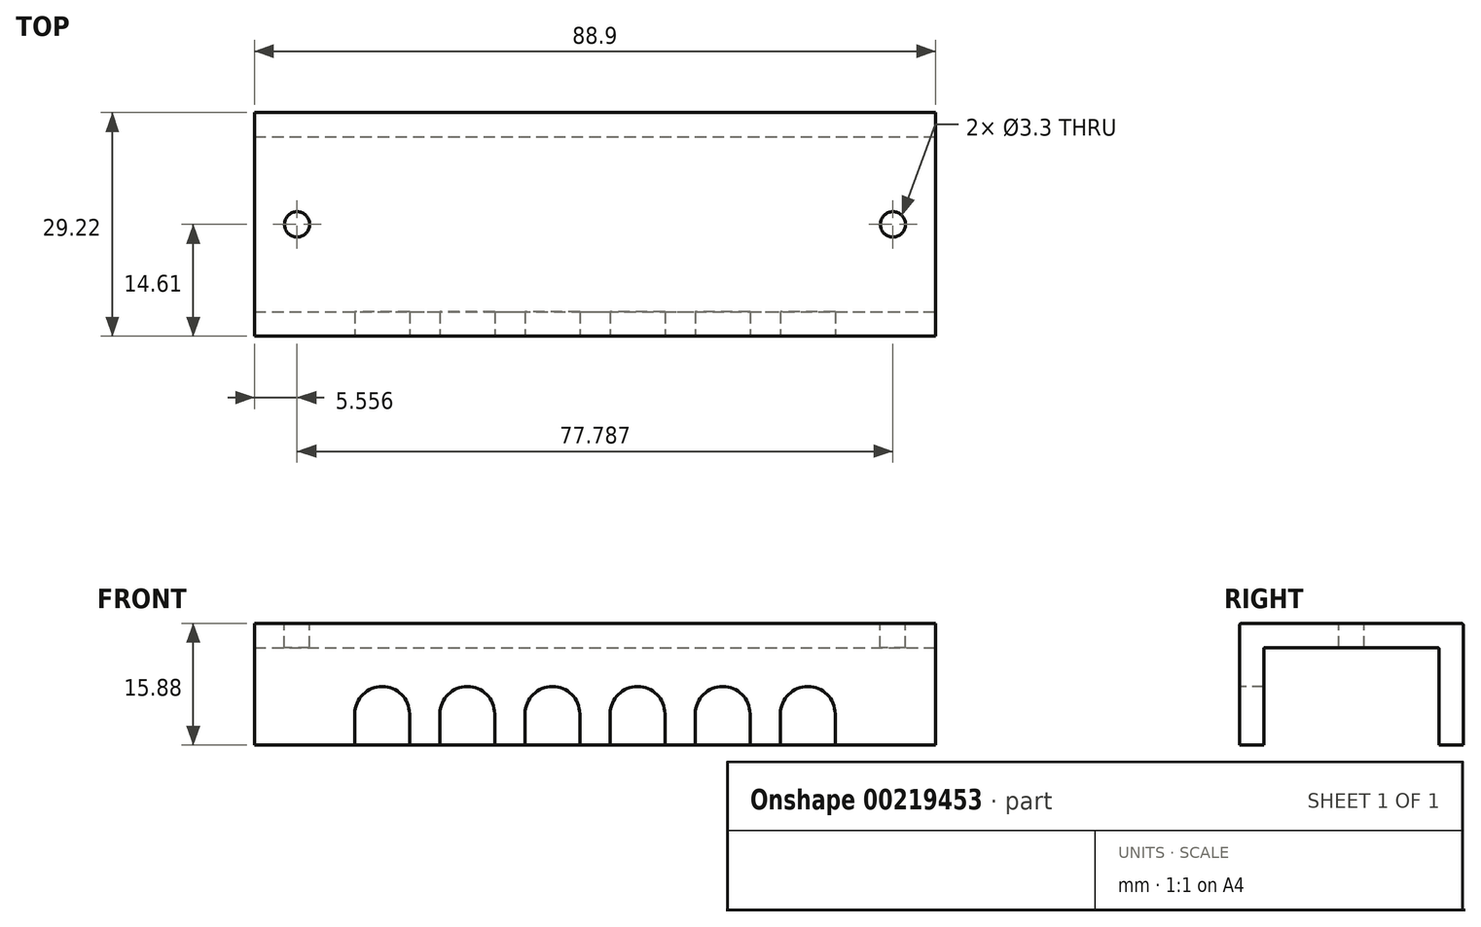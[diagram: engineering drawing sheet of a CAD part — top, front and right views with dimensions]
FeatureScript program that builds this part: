
annotation { "Feature Type Name" : "Feature", "Feature Type Description" : "" }
export const myFeature = defineFeature(function(context is Context, id is Id, definition is map)
    precondition{}
    {
        {
            assignVariable(context, id + "F0", {"name" : "MtrlThknss", "anyValue" : .125});
        }
        {
            var Q0;
            Q0=qCreatedBy(makeId("Top.planeOp"),FACE);
            var sketch = newSketch(context, id + "F1", { "sketchPlane" : qUnion([Q0])});
            skLineSegment(sketch, "E0.bottom", {"start": v(44.45, -14.6) * mm, "end": v(-44.45, -14.6) * mm});
            skLineSegment(sketch, "E0.top", {"start": v(44.45, 14.6) * mm, "end": v(-44.45, 14.6) * mm});
            skLineSegment(sketch, "E0.left", {"start": v(44.45, -14.6) * mm, "end": v(44.45, 14.6) * mm});
            skLineSegment(sketch, "E0.right", {"start": v(-44.45, -14.6) * mm, "end": v(-44.45, 14.6) * mm});
            skPoint(sketch, "E0.middle", {"position": v(0, 0) * mm});
            skSolve(sketch);
        }
        {
            var Q0;
            Q0=makeQuery(id+"F1.imprint","IMPRINT",FACE,{"disambiguationData":[TD([[makeQuery(id+"F1.imprint","IMPRINT",EDGE,{"derivedFrom":sQuery(id+"F1.wireOp",EDGE,"E0.bottom")}),-1.0]])]});
            extrude(context, id + "F2", {"entities" : qUnion([Q0]), "depth" : 3.17 * mm});
        }
        {
            var Q0;
            Q0=makeQuery(id+"F2.opExtrude","CAP_FACE",FACE,{"disambiguationData":[OSD([sQuery(id+"F1.wireOp",EDGE,"E0.bottom"),sQuery(id+"F1.wireOp",EDGE,"E0.top"),sQuery(id+"F1.wireOp",EDGE,"E0.left"),sQuery(id+"F1.wireOp",EDGE,"E0.right")])],"isStart":true});
            var sketch = newSketch(context, id + "F3", { "sketchPlane" : qUnion([Q0])});
            skLineSegment(sketch, "E1.bottom", {"start": v(-44.45, 14.6) * mm, "end": v(44.45, 14.6) * mm});
            skLineSegment(sketch, "E1.top", {"start": v(-44.45, 11.43) * mm, "end": v(44.45, 11.43) * mm});
            skLineSegment(sketch, "E1.left", {"start": v(-44.45, 14.6) * mm, "end": v(-44.45, 11.43) * mm});
            skLineSegment(sketch, "E1.right", {"start": v(44.45, 14.6) * mm, "end": v(44.45, 11.43) * mm});
            skLineSegment(sketch, "E2.bottom", {"start": v(-44.45, -14.6) * mm, "end": v(44.45, -14.6) * mm});
            skLineSegment(sketch, "E2.top", {"start": v(-44.45, -11.43) * mm, "end": v(44.45, -11.43) * mm});
            skLineSegment(sketch, "E2.left", {"start": v(-44.45, -14.6) * mm, "end": v(-44.45, -11.43) * mm});
            skLineSegment(sketch, "E2.right", {"start": v(44.45, -14.6) * mm, "end": v(44.45, -11.43) * mm});
            skSolve(sketch);
        }
        {
            var Q0;
            Q0=qSketchRegion(id+"F3",true);
            extrude(context, id + "F4", {"entities" : qUnion([Q0]), "operationType" : NewBodyOperationType.ADD, "depth" : 12.7 * mm});
        }
        {
            var Q0;
            Q0=makeQuery(id+"F2.opExtrude","CAP_FACE",FACE,{"disambiguationData":[OSD([sQuery(id+"F1.wireOp",EDGE,"E0.bottom"),sQuery(id+"F1.wireOp",EDGE,"E0.top"),sQuery(id+"F1.wireOp",EDGE,"E0.left"),sQuery(id+"F1.wireOp",EDGE,"E0.right")])],"isStart":false});
            var sketch = newSketch(context, id + "F5", { "sketchPlane" : qUnion([Q0])});
            skPoint(sketch, "E3", {"position": v(-38.9, 0) * mm});
            skPoint(sketch, "E4", {"position": v(38.9, 0) * mm});
            skSolve(sketch);
        }
        {
            var Q0;
            Q0=sQuery(id+"F5.wireOp",VERTEX,"E3");
            var Q1;
            Q1=sQuery(id+"F5.wireOp",VERTEX,"E4");
            var Q2;
            Q2=makeQuery(id+"F2.opExtrude","SWEPT_BODY",BODY,{"disambiguationData":[OSD([sQuery(id+"F1.wireOp",EDGE,"E0.bottom"),sQuery(id+"F1.wireOp",EDGE,"E0.top"),sQuery(id+"F1.wireOp",EDGE,"E0.left"),sQuery(id+"F1.wireOp",EDGE,"E0.right")])]});
            hole(context, id + "F6", {"style" : HoleStyle.SIMPLE, "endStyle" : HoleEndStyle.THROUGH, "standardTappedOrClearance" : lookupTablePath({ "standard" : "ISO", "fit" : "Normal", "size" : "M3", "type" : "Clearance" }), "standardBlindInLast" : lookupTablePath({ "fit" : "Standard", "standard" : "ISO", "size" : "M3", "type" : "Clearance" }), "holeDiameter" : 3.3 * mm, "locations" : qUnion([Q0, Q1]), "scope" : qUnion([Q2]), "isTappedThrough" : true});
        }
        {
            var Q0;
            Q0=makeQuery(id+"F4.boolean.opBoolean","MERGE",FACE,{"derivedFrom":[makeQuery(id+"F2.opExtrude","SWEPT_FACE",FACE,{"disambiguationData":[OSD([sQuery(id+"F1.wireOp",EDGE,"E0.bottom")])]}),makeQuery(id+"F4.opExtrude","SWEPT_FACE",FACE,{"disambiguationData":[OSD([sQuery(id+"F3.wireOp",EDGE,"E1.bottom")])]})]});
            var sketch = newSketch(context, id + "F7", { "sketchPlane" : qUnion([Q0])});
            skCircle(sketch, "E5", {"center": v(-27.78, -8.64) * mm, "radius": 3.57 * mm});
            skCircle(sketch, "E6", {"center": v(-16.67, -8.64) * mm, "radius": 3.57 * mm});
            skCircle(sketch, "E7", {"center": v(-5.56, -8.64) * mm, "radius": 3.57 * mm});
            skCircle(sketch, "E8", {"center": v(5.56, -8.64) * mm, "radius": 3.57 * mm});
            skCircle(sketch, "E9", {"center": v(16.67, -8.64) * mm, "radius": 3.57 * mm});
            skCircle(sketch, "E10", {"center": v(27.78, -8.64) * mm, "radius": 3.57 * mm});
            skLineSegment(sketch, "E11.bottom", {"start": v(-31.35, -12.7) * mm, "end": v(-24.2, -12.7) * mm});
            skLineSegment(sketch, "E11.top", {"start": v(-31.35, -8.64) * mm, "end": v(-24.2, -8.64) * mm});
            skLineSegment(sketch, "E11.left", {"start": v(-31.35, -12.7) * mm, "end": v(-31.35, -8.64) * mm});
            skLineSegment(sketch, "E11.right", {"start": v(-24.2, -12.7) * mm, "end": v(-24.2, -8.64) * mm});
            skLineSegment(sketch, "E12.bottom", {"start": v(-20.24, -8.64) * mm, "end": v(-13.1, -8.64) * mm});
            skLineSegment(sketch, "E12.top", {"start": v(-20.24, -12.7) * mm, "end": v(-13.1, -12.7) * mm});
            skLineSegment(sketch, "E12.left", {"start": v(-20.24, -8.64) * mm, "end": v(-20.24, -12.7) * mm});
            skLineSegment(sketch, "E12.right", {"start": v(-13.1, -8.64) * mm, "end": v(-13.1, -12.7) * mm});
            skLineSegment(sketch, "E13.bottom", {"start": v(-9.13, -8.64) * mm, "end": v(-1.98, -8.64) * mm});
            skLineSegment(sketch, "E13.top", {"start": v(-9.13, -12.7) * mm, "end": v(-1.98, -12.7) * mm});
            skLineSegment(sketch, "E13.left", {"start": v(-9.13, -8.64) * mm, "end": v(-9.13, -12.7) * mm});
            skLineSegment(sketch, "E13.right", {"start": v(-1.98, -8.64) * mm, "end": v(-1.98, -12.7) * mm});
            skLineSegment(sketch, "E14.bottom", {"start": v(1.98, -8.64) * mm, "end": v(9.13, -8.64) * mm});
            skLineSegment(sketch, "E14.top", {"start": v(1.98, -12.7) * mm, "end": v(9.13, -12.7) * mm});
            skLineSegment(sketch, "E14.left", {"start": v(1.98, -8.64) * mm, "end": v(1.98, -12.7) * mm});
            skLineSegment(sketch, "E14.right", {"start": v(9.13, -8.64) * mm, "end": v(9.13, -12.7) * mm});
            skLineSegment(sketch, "E15.bottom", {"start": v(13.1, -8.64) * mm, "end": v(20.24, -8.64) * mm});
            skLineSegment(sketch, "E15.top", {"start": v(13.1, -12.7) * mm, "end": v(20.24, -12.7) * mm});
            skLineSegment(sketch, "E15.left", {"start": v(13.1, -8.64) * mm, "end": v(13.1, -12.7) * mm});
            skLineSegment(sketch, "E15.right", {"start": v(20.24, -8.64) * mm, "end": v(20.24, -12.7) * mm});
            skLineSegment(sketch, "E16.bottom", {"start": v(24.2, -8.64) * mm, "end": v(31.35, -8.64) * mm});
            skLineSegment(sketch, "E16.top", {"start": v(24.2, -12.7) * mm, "end": v(31.35, -12.7) * mm});
            skLineSegment(sketch, "E16.left", {"start": v(24.2, -8.64) * mm, "end": v(24.2, -12.7) * mm});
            skLineSegment(sketch, "E16.right", {"start": v(31.35, -8.64) * mm, "end": v(31.35, -12.7) * mm});
            skSolve(sketch);
        }
        {
            var Q0;
            Q0=qSketchRegion(id+"F7",true);
            extrude(context, id + "F8", {"entities" : qUnion([Q0]), "operationType" : NewBodyOperationType.REMOVE, "oppositeDirection" : true, "depth" : 3.17 * mm});
        }
        {
            var Q0;
            Q0=makeQuery(id+"F2.opExtrude","CAP_EDGE",EDGE,{"disambiguationData":[OSD([sQuery(id+"F1.wireOp",EDGE,"E0.bottom")])],"isStart":false});
            var Q1;
            Q1=makeQuery(id+"F2.opExtrude","CAP_EDGE",EDGE,{"disambiguationData":[OSD([sQuery(id+"F1.wireOp",EDGE,"E0.top")])],"isStart":false});
            fillet(context, id + "F9", {"entities" : qUnion([Q0, Q1]), "radius" : (2 * getVariable(context, 'MtrlThknss')) * mm, "tangentPropagation" : true});
        }
        {
            var Q0;
            Q0=makeQuery(id+"F4.opExtrude","CAP_EDGE",EDGE,{"disambiguationData":[OSD([sQuery(id+"F3.wireOp",EDGE,"E2.top")])],"isStart":true});
            var Q1;
            Q1=makeQuery(id+"F4.opExtrude","CAP_EDGE",EDGE,{"disambiguationData":[OSD([sQuery(id+"F3.wireOp",EDGE,"E1.top")])],"isStart":true});
            fillet(context, id + "F10", {"entities" : qUnion([Q0, Q1]), "radius" : (getVariable(context, 'MtrlThknss')) * mm, "tangentPropagation" : true});
        }
    });
